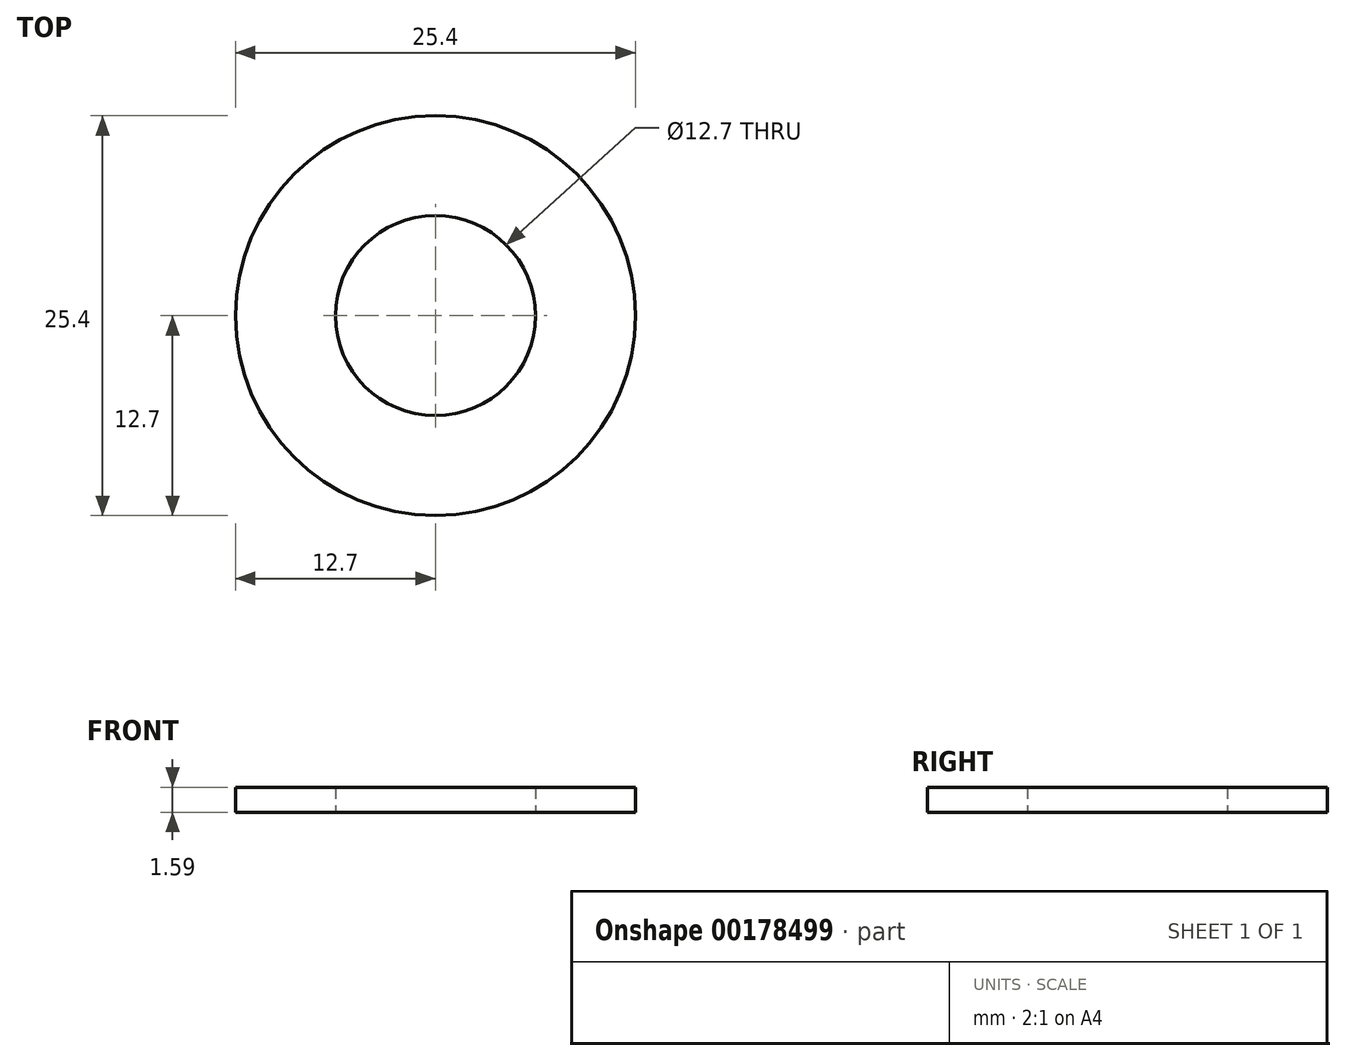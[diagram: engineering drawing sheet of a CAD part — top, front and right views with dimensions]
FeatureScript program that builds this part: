
annotation { "Feature Type Name" : "Feature", "Feature Type Description" : "" }
export const myFeature = defineFeature(function(context is Context, id is Id, definition is map)
    precondition{}
    {
        {
            var Q0;
            Q0=qCreatedBy(makeId("Top.planeOp"),FACE);
            var sketch = newSketch(context, id + "F0", { "sketchPlane" : qUnion([Q0])});
            skCircle(sketch, "E0", {"center": v(0, 0) * mm, "radius": 6.35 * mm});
            skCircle(sketch, "E1", {"center": v(0, 0) * mm, "radius": 12.7 * mm});
            skSolve(sketch);
        }
        {
            var Q0;
            Q0=makeQuery(id+"F0.imprint","IMPRINT",FACE,{"disambiguationData":[TD([[makeQuery(id+"F0.imprint","IMPRINT",EDGE,{"derivedFrom":sQuery(id+"F0.wireOp",EDGE,"E0")}),-1.0]])]});
            extrude(context, id + "F1", {"entities" : qUnion([Q0]), "depth" : 1.59 * mm});
        }
    });
